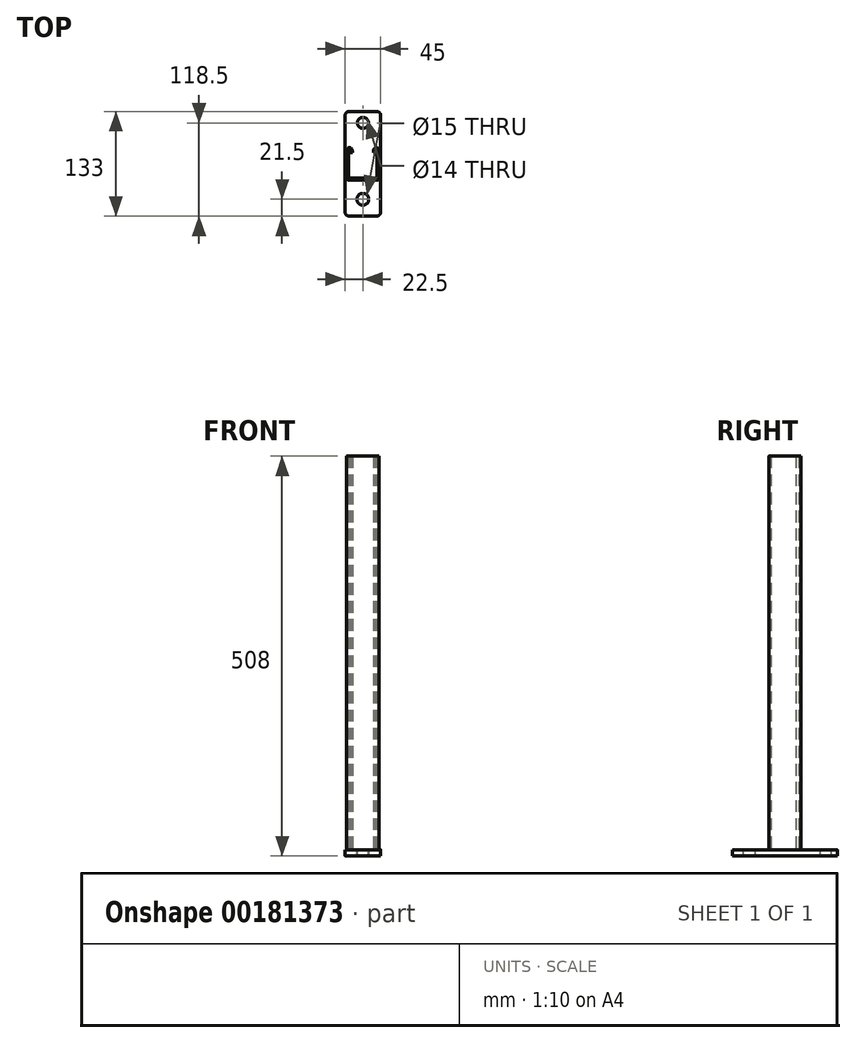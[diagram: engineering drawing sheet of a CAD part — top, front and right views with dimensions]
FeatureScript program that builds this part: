
annotation { "Feature Type Name" : "Feature", "Feature Type Description" : "" }
export const myFeature = defineFeature(function(context is Context, id is Id, definition is map)
    precondition{}
    {
        {
            var Q0;
            Q0=qCreatedBy(makeId("Top.planeOp"),FACE);
            var sketch = newSketch(context, id + "F0", { "sketchPlane" : qUnion([Q0])});
            skLineSegment(sketch, "E0.top", {"start": v(-20.5, -20.5) * mm, "end": v(20.5, -20.5) * mm});
            skLineSegment(sketch, "E0.left", {"start": v(-20.5, 17) * mm, "end": v(-20.5, -20.5) * mm});
            skLineSegment(sketch, "E0.right", {"start": v(20.5, 17) * mm, "end": v(20.5, -20.5) * mm});
            skPoint(sketch, "E0.middle", {"position": v(0, 0) * mm});
            skLineSegment(sketch, "E1.0", {"start": v(18, 17) * mm, "end": v(18, -18) * mm});
            skLineSegment(sketch, "E1.1", {"start": v(-18, -18) * mm, "end": v(18, -18) * mm});
            skArc(sketch, "E2", {"start": v(-13.5, 17) * mm, "mid": v(-17, 20.5) * mm, "end": v(-20.5, 17) * mm});
            skArc(sketch, "E3", {"start": v(20.5, 17) * mm, "mid": v(17, 20.5) * mm, "end": v(13.5, 17) * mm});
            skLineSegment(sketch, "E4.bottom", {"start": v(-13.5, 14) * mm, "end": v(-16, 14) * mm});
            skLineSegment(sketch, "E4.top", {"start": v(-13.5, 17) * mm, "end": v(-16, 17) * mm});
            skLineSegment(sketch, "E4.left", {"start": v(-13.5, 14) * mm, "end": v(-13.5, 17) * mm});
            skLineSegment(sketch, "E4.right", {"start": v(-16, 14) * mm, "end": v(-16, 17) * mm});
            skPoint(sketch, "E4.middle", {"position": v(-14.75, 15.5) * mm});
            skLineSegment(sketch, "E5.bottom", {"start": v(16, 14) * mm, "end": v(13.5, 14) * mm});
            skLineSegment(sketch, "E5.left", {"start": v(16, 14) * mm, "end": v(16, 17) * mm});
            skLineSegment(sketch, "E5.right", {"start": v(13.5, 14) * mm, "end": v(13.5, 17) * mm});
            skPoint(sketch, "E5.middle", {"position": v(14.75, 15.5) * mm});
            skArc(sketch, "E6.0", {"start": v(-16, 17) * mm, "mid": v(-17, 18) * mm, "end": v(-18, 17) * mm});
            skArc(sketch, "E7.0", {"start": v(18, 17) * mm, "mid": v(17, 18) * mm, "end": v(16, 17) * mm});
            skPoint(sketch, "E8.orphan", {"position": v(20.5, 20.5) * mm});
            skPoint(sketch, "E9.orphan", {"position": v(-20.5, 20.5) * mm});
            skLineSegment(sketch, "E10.trimOffspring", {"start": v(-18, 17) * mm, "end": v(-18, -18) * mm});
            skSolve(sketch);
        }
        {
            var Q0;
            Q0 = qSketchRegion(id + "F0", true);
            extrude(context, id + "F1", {"entities" : qUnion([Q0]), "depth" : 500 * mm});
        }
        {
            var Q0;
            Q0=makeQuery(id+"F1.opExtrude","SWEPT_EDGE",EDGE,{"disambiguationData":[OSD([sQuery(id+"F0.wireOp",EDGE,"E0.top"),sQuery(id+"F0.wireOp",EDGE,"E0.left")])]});
            var Q1;
            Q1=makeQuery(id+"F1.opExtrude","SWEPT_EDGE",EDGE,{"disambiguationData":[OSD([sQuery(id+"F0.wireOp",EDGE,"E0.top"),sQuery(id+"F0.wireOp",EDGE,"E0.right")])]});
            var Q2;
            Q2=makeQuery(id+"F1.opExtrude","SWEPT_EDGE",EDGE,{"disambiguationData":[OSD([sQuery(id+"F0.wireOp",EDGE,"E1.1"),sQuery(id+"F0.wireOp",EDGE,"E10.trimOffspring")])]});
            var Q3;
            Q3=makeQuery(id+"F1.opExtrude","SWEPT_EDGE",EDGE,{"disambiguationData":[OSD([sQuery(id+"F0.wireOp",EDGE,"E1.0"),sQuery(id+"F0.wireOp",EDGE,"E1.1")])]});
            fillet(context, id + "F2", {"entities" : qUnion([Q0, Q1, Q2, Q3]), "radius" : 2 * mm, "tangentPropagation" : true, "allowEdgeOverflow" : false});
        }
        {
            var Q0;
            Q0=makeQuery(id+"F1.opExtrude","CAP_FACE",FACE,{"disambiguationData":[OSD([sQuery(id+"F0.wireOp",EDGE,"E0.top"),sQuery(id+"F0.wireOp",EDGE,"E0.left"),sQuery(id+"F0.wireOp",EDGE,"E0.right"),sQuery(id+"F0.wireOp",EDGE,"E1.0"),sQuery(id+"F0.wireOp",EDGE,"E1.1"),sQuery(id+"F0.wireOp",EDGE,"E2"),sQuery(id+"F0.wireOp",EDGE,"E3"),sQuery(id+"F0.wireOp",EDGE,"E4.bottom"),sQuery(id+"F0.wireOp",EDGE,"E4.left"),sQuery(id+"F0.wireOp",EDGE,"E4.right"),sQuery(id+"F0.wireOp",EDGE,"E5.bottom"),sQuery(id+"F0.wireOp",EDGE,"E5.left"),sQuery(id+"F0.wireOp",EDGE,"E5.right"),sQuery(id+"F0.wireOp",EDGE,"E6.0"),sQuery(id+"F0.wireOp",EDGE,"E7.0"),sQuery(id+"F0.wireOp",EDGE,"E10.trimOffspring")])],"isStart":true});
            var sketch = newSketch(context, id + "F3", { "sketchPlane" : qUnion([Q0])});
            skLineSegment(sketch, "E11.bottom", {"start": v(-17.5, 66.5) * mm, "end": v(17.5, 66.5) * mm});
            skLineSegment(sketch, "E11.top", {"start": v(-17.5, -66.5) * mm, "end": v(17.5, -66.5) * mm});
            skLineSegment(sketch, "E11.left", {"start": v(-22.5, 61.5) * mm, "end": v(-22.5, -61.5) * mm});
            skLineSegment(sketch, "E11.right", {"start": v(22.5, 61.5) * mm, "end": v(22.5, -61.5) * mm});
            skPoint(sketch, "E12.visualSharp", {"position": v(-22.5, 66.5) * mm});
            skArc(sketch, "E12.filletArc", {"start": v(-17.5, 66.5) * mm, "mid": v(-21.04, 65.04) * mm, "end": v(-22.5, 61.5) * mm});
            skPoint(sketch, "E13.visualSharp", {"position": v(22.5, 66.5) * mm});
            skArc(sketch, "E13.filletArc", {"start": v(22.5, 61.5) * mm, "mid": v(21.04, 65.04) * mm, "end": v(17.5, 66.5) * mm});
            skPoint(sketch, "E14.visualSharp", {"position": v(22.5, -66.5) * mm});
            skArc(sketch, "E14.filletArc", {"start": v(17.5, -66.5) * mm, "mid": v(21.04, -65.04) * mm, "end": v(22.5, -61.5) * mm});
            skPoint(sketch, "E15.visualSharp", {"position": v(-22.5, -66.5) * mm});
            skArc(sketch, "E15.filletArc", {"start": v(-22.5, -61.5) * mm, "mid": v(-21.04, -65.04) * mm, "end": v(-17.5, -66.5) * mm});
            skCircle(sketch, "E16", {"center": v(0, 45) * mm, "radius": 7.5 * mm});
            skCircle(sketch, "E17", {"center": v(0, -52) * mm, "radius": 7 * mm});
            skSolve(sketch);
        }
        {
            var Q0;
            Q0 = qSketchRegion(id + "F3", true);
            extrude(context, id + "F4", {"entities" : qUnion([Q0]), "operationType" : NewBodyOperationType.ADD, "depth" : 8 * mm});
        }
    });
